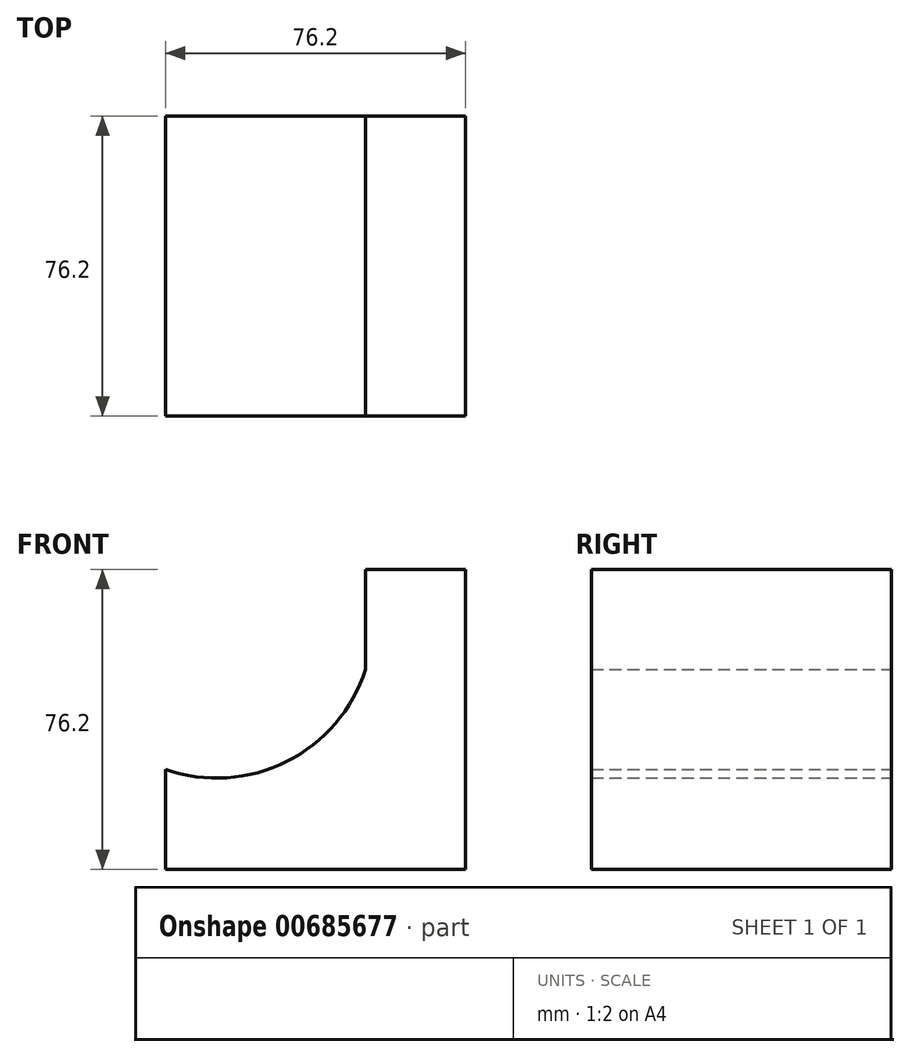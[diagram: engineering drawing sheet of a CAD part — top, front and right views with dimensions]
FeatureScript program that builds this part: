
annotation { "Feature Type Name" : "Feature", "Feature Type Description" : "" }
export const myFeature = defineFeature(function(context is Context, id is Id, definition is map)
    precondition{}
    {
        {
            var Q0;
            Q0=qCreatedBy(makeId("Front.planeOp"),FACE);
            var sketch = newSketch(context, id + "F0", { "sketchPlane" : qUnion([Q0])});
            skLineSegment(sketch, "E0", {"start": v(0, 0) * mm, "end": v(0, 25.4) * mm});
            skLineSegment(sketch, "E1", {"start": v(0, 25.4) * mm, "end": v(25.4, 25.4) * mm});
            skLineSegment(sketch, "E2", {"start": v(25.4, 25.4) * mm, "end": v(25.4, -50.8) * mm});
            skLineSegment(sketch, "E3", {"start": v(25.4, -50.8) * mm, "end": v(-50.8, -50.8) * mm});
            skLineSegment(sketch, "E4", {"start": v(-50.8, -50.8) * mm, "end": v(-50.8, -25.4) * mm});
            skArc(sketch, "E5", {"start": v(-50.8, -25.4) * mm, "mid": v(-20.05, -23.4) * mm, "end": v(0, 0) * mm});
            skSolve(sketch);
        }
        {
            var Q0;
            Q0 = qSketchRegion(id + "F0", true);
            extrude(context, id + "F1", {"entities" : qUnion([Q0]), "depth" : 76.2 * mm, "offsetDistance" : 25.4 * mm});
        }
    });
